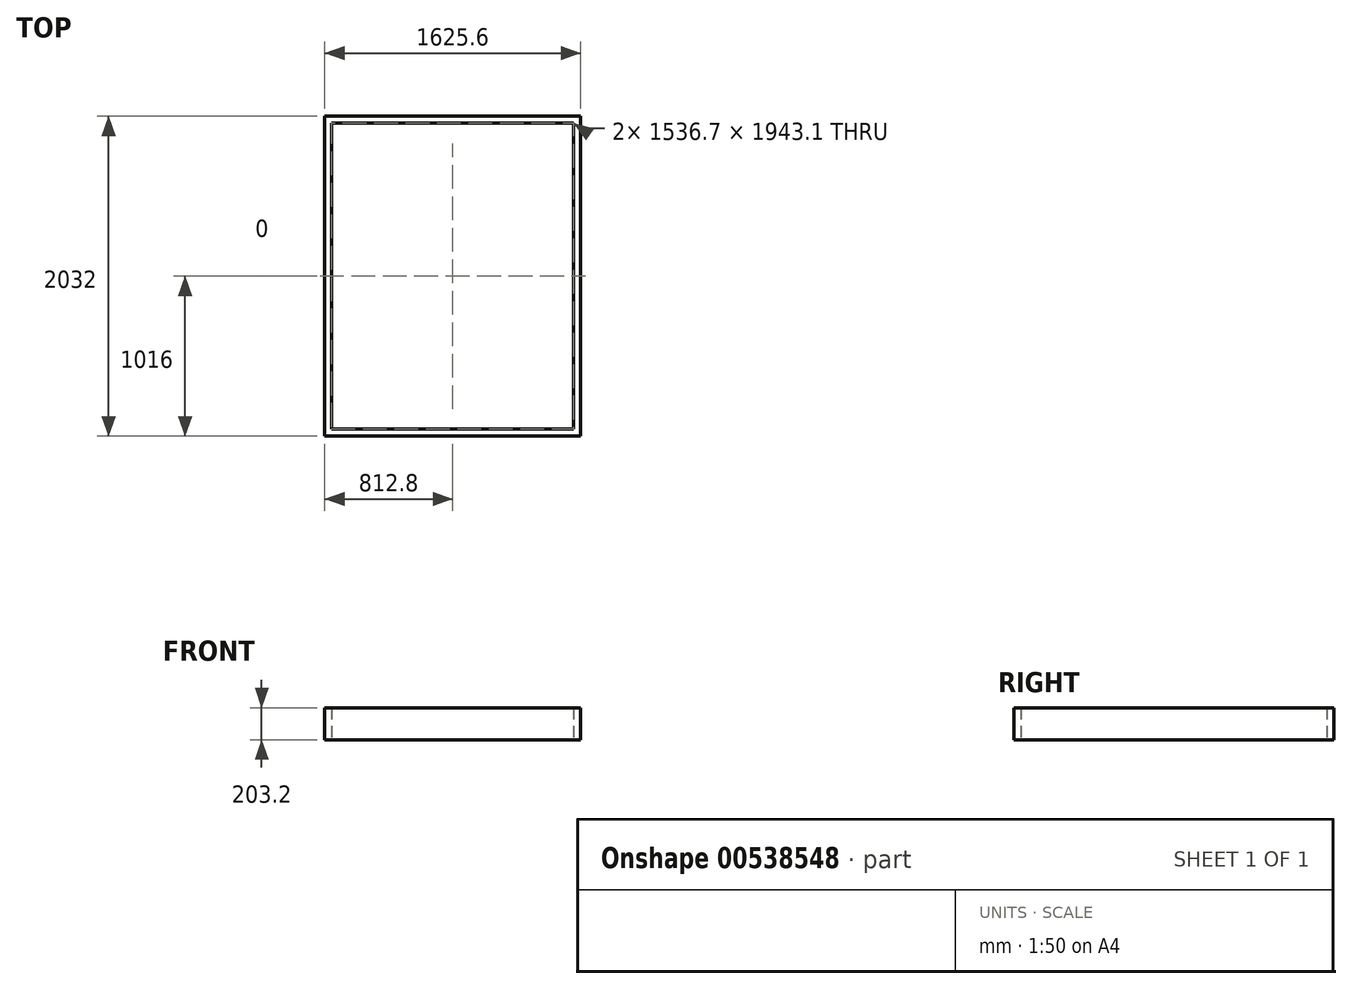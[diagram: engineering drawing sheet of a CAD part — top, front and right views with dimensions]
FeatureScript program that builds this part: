
annotation { "Feature Type Name" : "Feature", "Feature Type Description" : "" }
export const myFeature = defineFeature(function(context is Context, id is Id, definition is map)
    precondition{}
    {
        {
            var Q0;
            Q0=qCreatedBy(makeId("Top.planeOp"),FACE);
            var sketch = newSketch(context, id + "F0", { "sketchPlane" : qUnion([Q0])});
            skLineSegment(sketch, "E0.bottom", {"start": v(-812.8, 1016) * mm, "end": v(812.8, 1016) * mm});
            skLineSegment(sketch, "E0.top", {"start": v(-812.8, -1016) * mm, "end": v(812.8, -1016) * mm});
            skLineSegment(sketch, "E0.left", {"start": v(-812.8, 1016) * mm, "end": v(-812.8, -1016) * mm});
            skLineSegment(sketch, "E0.right", {"start": v(812.8, 1016) * mm, "end": v(812.8, -1016) * mm});
            skPoint(sketch, "E0.middle", {"position": v(0, 0) * mm});
            skLineSegment(sketch, "E1.bottom", {"start": v(-768.35, 971.55) * mm, "end": v(768.35, 971.55) * mm});
            skLineSegment(sketch, "E1.top", {"start": v(-768.35, -971.55) * mm, "end": v(768.35, -971.55) * mm});
            skLineSegment(sketch, "E1.left", {"start": v(-768.35, 971.55) * mm, "end": v(-768.35, -971.55) * mm});
            skLineSegment(sketch, "E1.right", {"start": v(768.35, 971.55) * mm, "end": v(768.35, -971.55) * mm});
            skSolve(sketch);
        }
        {
            var Q0;
            Q0 = qSketchRegion(id + "F0", true);
            extrude(context, id + "F1", {"entities" : qUnion([Q0]), "depth" : 203.2 * mm, "offsetDistance" : 25.4 * mm});
        }
    });
